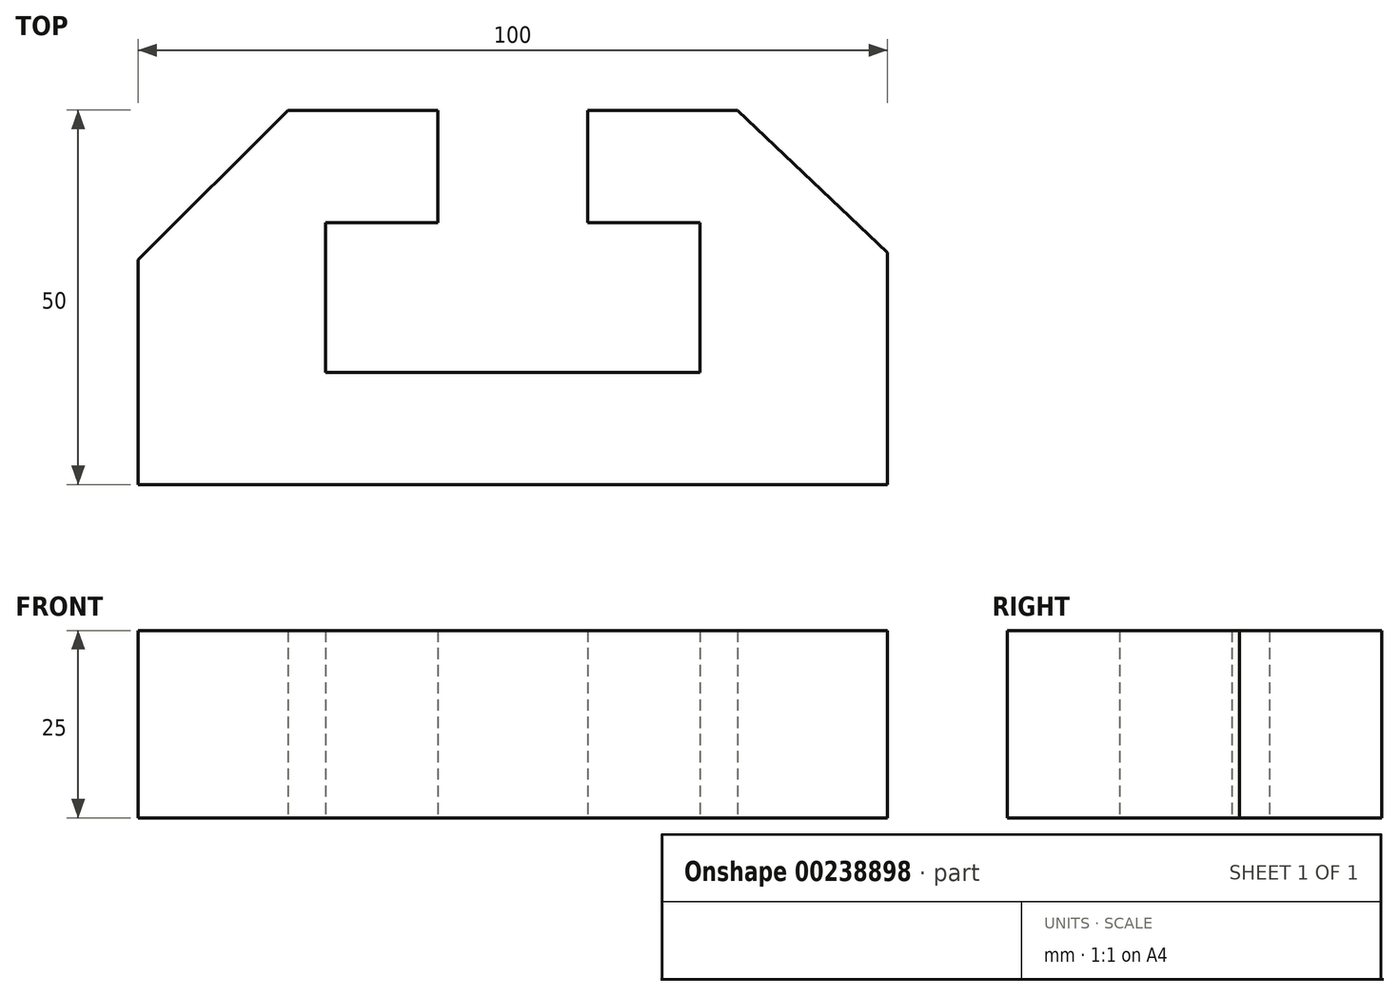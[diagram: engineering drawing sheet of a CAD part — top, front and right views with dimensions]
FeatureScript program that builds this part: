
annotation { "Feature Type Name" : "Feature", "Feature Type Description" : "" }
export const myFeature = defineFeature(function(context is Context, id is Id, definition is map)
    precondition{}
    {
        {
            var Q0;
            Q0=qCreatedBy(makeId("Top.planeOp"),FACE);
            var sketch = newSketch(context, id + "F0", { "sketchPlane" : qUnion([Q0])});
            skLineSegment(sketch, "E0", {"start": v(-51.41, -49.12) * mm, "end": v(48.59, -49.12) * mm});
            skLineSegment(sketch, "E1", {"start": v(-51.41, -49.12) * mm, "end": v(-51.41, -19.12) * mm});
            skLineSegment(sketch, "E2", {"start": v(-51.41, -19.12) * mm, "end": v(-31.41, 0.88) * mm});
            skLineSegment(sketch, "E3", {"start": v(-31.41, 0.88) * mm, "end": v(-11.41, 0.88) * mm});
            skLineSegment(sketch, "E4", {"start": v(-11.41, 0.88) * mm, "end": v(-11.41, -14.12) * mm});
            skLineSegment(sketch, "E5", {"start": v(-11.41, -14.12) * mm, "end": v(-26.41, -14.12) * mm});
            skLineSegment(sketch, "E6", {"start": v(-26.41, -14.12) * mm, "end": v(-26.41, -34.12) * mm});
            skLineSegment(sketch, "E7", {"start": v(-26.41, -34.12) * mm, "end": v(23.59, -34.12) * mm});
            skLineSegment(sketch, "E8", {"start": v(23.59, -34.12) * mm, "end": v(23.59, -14.12) * mm});
            skLineSegment(sketch, "E9", {"start": v(23.59, -14.12) * mm, "end": v(8.59, -14.12) * mm});
            skLineSegment(sketch, "E10", {"start": v(8.59, -14.12) * mm, "end": v(8.59, 0.88) * mm});
            skLineSegment(sketch, "E11", {"start": v(8.59, 0.88) * mm, "end": v(28.59, 0.88) * mm});
            skLineSegment(sketch, "E12", {"start": v(28.59, 0.88) * mm, "end": v(48.59, -18.12) * mm});
            skLineSegment(sketch, "E13", {"start": v(48.59, -18.12) * mm, "end": v(48.59, -49.12) * mm});
            skSolve(sketch);
        }
        {
            var Q0;
            Q0=makeQuery(id+"F0.imprint","IMPRINT",FACE,{"disambiguationData":[TD([[makeQuery(id+"F0.imprint","IMPRINT",EDGE,{"derivedFrom":sQuery(id+"F0.wireOp",EDGE,"E0")}),1.0]])]});
            extrude(context, id + "F1", {"entities" : qUnion([Q0]), "depth" : 25 * mm});
        }
    });
